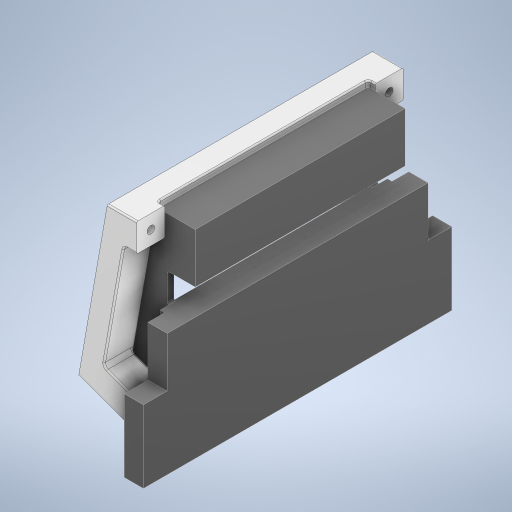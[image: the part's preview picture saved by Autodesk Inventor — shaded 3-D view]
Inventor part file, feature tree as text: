
AUTODESK INVENTOR PART (.ipt)
format: ipt  version: 2024 (Build 280153000, 153)  size: 685,568 bytes
history: native  units: mm
features: sketch x15, extrude x14, projected_geometry x11, fillet x9, plane x6, hole x4, mirror x2, other x1
ambient origin geometry x8: Origin, YZ Plane, XZ Plane, XY Plane, X Axis, Y Axis, Z Axis, Center Point
bodies: Solid1 (feature_tree)
feature tree (62):
  extrude  "Extrusion1"  Depth=20.0mm
  plane  "Work Plane1"
  extrude  "Extrusion2"  Depth=17.453293mm
  extrude  "Extrusion3"  Depth=20.0mm
  extrude  "Extrusion4"  Depth=190.0mm TaperAngle=0.0deg
  plane  "Work Plane2"
  sketch  "Sketch9"  dims[d15=-12.0mm d16=2.0mm]
  extrude  "Extrusion7"  Depth=2.0mm
  extrude  "Extrusion8"  Depth=1.0mm
  fillet  "Fillet14"  Radius=20.0mm
  fillet  "Fillet9"  Radius=5.0mm
  fillet  "Fillet10"  Radius=16.0mm
  fillet  "Fillet11"  Radius=1.0mm
  fillet  "Fillet12"  Radius=8.0mm
  fillet  "Fillet13"  Radius=154.9mm
  fillet  "Fillet16"  Radius=92.0mm
  hole  "Hole4"  [1 undecoded]
  plane  "Work Plane3"
  hole  "Hole5"  [1 undecoded]
  sketch  "Sketch14"  dims[d57=3.0mm d58=6.0mm d59=4.0mm d60=2.0mm d61=90.0deg d62=8.0mm d63=0.0mm]
  plane  "Work Plane4"
  plane  "Work Plane5"
  extrude  "Extrusion9"  Depth=1.0mm
  sketch  "Sketch15"  dims[d64=6.0mm d65=6.0mm d66=4.0mm d67=2.0mm d68=90.0deg d69=10.0mm d70=0.0mm d73=1.0mm]
  plane  "Work Plane6"
  extrude  "Extrusion10"  Depth=10.0mm
  extrude  "Extrusion11"  Depth=1.0mm
  mirror  "Mirror1"
  fillet  "Fillet17"  [1 undecoded]
  extrude  "Extrusion12"  Depth=1.0mm
  extrude  "Extrusion13"  Depth=1.0mm
  mirror  "Mirror2"
  extrude  "Extrusion14"  Depth=10.0mm
  fillet  "Fillet18"  Radius=20.0mm
  extrude  "Extrusion15"  Depth=10.0mm
  extrude  "Extrusion16"  Depth=10.0mm
  hole  "Hole2"  [1 undecoded]
  hole  "Hole3"  [1 undecoded]
  sketch  "Sketch1"  dims[d6=118.0mm d7=20.0mm]
  sketch  "Sketch2"  dims[d8=15.0mm d9=17.453293mm]
  projected_geometry  "Projected Loop1"
  sketch  "Sketch3"  dims[d10=17.453293mm d11=20.0mm]
  projected_geometry  "Projected Loop2"
  sketch  "Sketch4"  dims[d12=16.0mm d13=190.0mm d14=0.0mm]
  projected_geometry  "Projected Loop3"
  sketch  "Sketch10"  dims[d17=190.0mm d18=0.0mm d19=20.0mm d20=20.0mm d21=5.0mm d22=0.0mm d25=16.0mm d26=1.0mm d27=0.0mm d45=8.0mm d48=154.9mm d49=92.0mm]
  sketch  "Sketch11"  dims[d50=3.34mm d51=2.15mm]
  sketch  "Sketch12"  dims[d52=140.0mm d53=0.0mm d54=5.0mm]
  sketch  "Sketch13"  dims[d55=150.0mm d56=0.0mm]
  projected_geometry  "Projected Loop6"
  projected_geometry  "Projected Loop7"
  sketch  "Sketch16"  dims[d74=3.0mm d75=10.0mm]
  other  "Rear Cover"
  projected_geometry  "Projected Loop9"
  sketch  "Sketch17"  dims[d76=2.0mm d77=1.0mm]
  projected_geometry  "Projected Loop10"
  sketch  "Sketch18"  dims[d80=5.4mm d81=6.0mm d82=4.0mm d83=2.0mm d84=90.0deg d85=10.0mm d86=0.0mm d87=-5.0mm]
  projected_geometry  "Projected Loop11"
  projected_geometry  "Projected Loop12"
  sketch  "Sketch19"  dims[d88=9.5mm d89=6.0mm d90=4.0mm d91=2.0mm d92=90.0deg d93=8.0mm d94=0.0mm d95=1.0mm d97=1.0mm d98=20.0mm d99=20.0mm d100=4.25mm d101=45.75mm d102=20.0mm d104=21.7mm d105=32.945242mm d106=0.2mm d107=0.4mm d108=0.2mm d109=0.2mm d110=1.0mm d111=0.2mm d112=0.4mm d113=0.4mm d114=0.4mm d115=8.0mm d116=3.25mm d117=12.0mm d118=3.0mm d119=3.0mm d120=3.0mm d121=10.0mm d122=0.0mm d123=0.2mm d124=-4.25mm d125=10.0mm d126=0.0mm d127=10.0mm d128=0.0mm d129=1.2mm d131=3.0mm d132=6.0mm d133=6.0mm d134=10.0mm d135=0.0mm d136=12.0mm d137=12.0mm d138=12.0mm d139=12.0mm d140=10.0mm d141=0.0mm d142=0.4mm d143=10.0mm d144=0.0mm d145=2.0mm d146=3.0mm d147=7.0mm d148=140.0mm d149=0.0mm d150=0.0mm d151=0.0mm]
  projected_geometry  "Project Cut Edges1"
  projected_geometry  "Project Cut Edges2"
note: 5 required parameter values undecoded (feature->parameter linkage not recoverable at this tier; creation-order binding heuristic only, values carry confidence <= 0.55)
